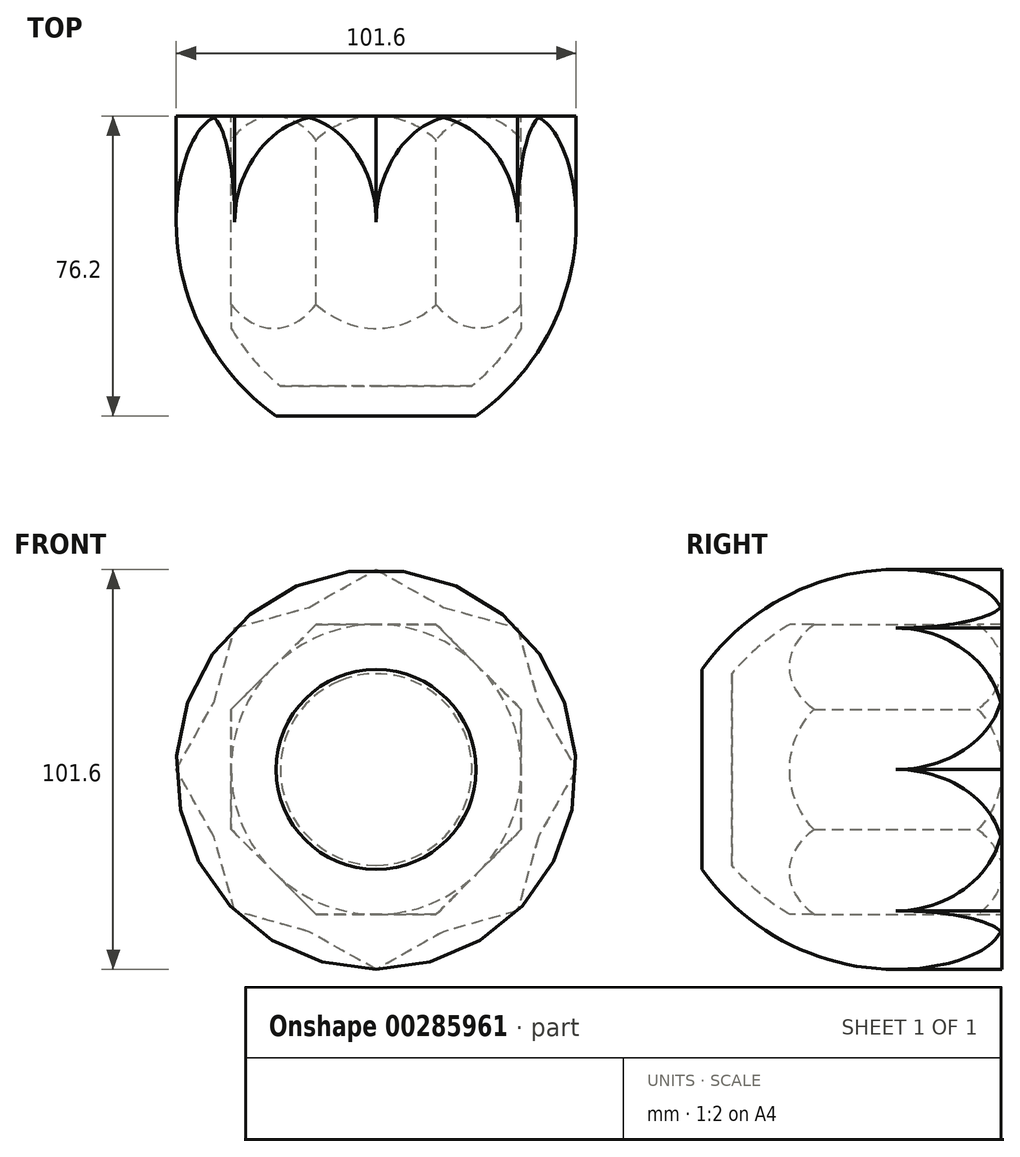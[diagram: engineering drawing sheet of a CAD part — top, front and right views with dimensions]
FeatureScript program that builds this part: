
annotation { "Feature Type Name" : "Feature", "Feature Type Description" : "" }
export const myFeature = defineFeature(function(context is Context, id is Id, definition is map)
    precondition{}
    {
        {
            var Q0;
            Q0=qCreatedBy(makeId("Top.planeOp"),FACE);
            var sketch = newSketch(context, id + "F0", { "sketchPlane" : qUnion([Q0])});
            skLineSegment(sketch, "E0", {"start": v(0, 0) * mm, "end": v(0, 76.2) * mm, "construction": true});
            skLineSegment(sketch, "E1", {"start": v(0, 76.2) * mm, "end": v(44.45, 76.2) * mm, "construction": true});
            skLineSegment(sketch, "E2", {"start": v(0, 0) * mm, "end": v(25.4, 0) * mm});
            skArc(sketch, "E3", {"start": v(25.4, 0) * mm, "mid": v(49, 34.58) * mm, "end": v(44.45, 76.2) * mm});
            skLineSegment(sketch, "E4", {"start": v(50.8, 0) * mm, "end": v(50.8, 76.2) * mm, "construction": true});
            skLineSegment(sketch, "E5", {"start": v(44.45, 76.2) * mm, "end": v(36.83, 76.2) * mm});
            skLineSegment(sketch, "E6", {"start": v(0, 0) * mm, "end": v(0, 7.62) * mm});
            skLineSegment(sketch, "E7", {"start": v(0, 7.62) * mm, "end": v(24.33, 7.62) * mm});
            skArc(sketch, "E8", {"start": v(24.33, 7.62) * mm, "mid": v(43.22, 39.6) * mm, "end": v(36.83, 76.2) * mm});
            skSolve(sketch);
        }
        {
            var Q0;
            Q0 = qSketchRegion(id + "F0", true);
            var Q1;
            Q1=sQuery(id+"F0.wireOp",EDGE,"E0");
            revolve(context, id + "F1", {"entities" : qUnion([Q0]), "axis" : qUnion([Q1]), "revolveType" : RevolveType.FULL});
        }
        {
            var Q0;
            Q0=makeQuery(id+"F1.opRevolve","SWEPT_FACE",FACE,{"disambiguationData":[OSD([sQuery(id+"F0.wireOp",EDGE,"E5")])]});
            var sketch = newSketch(context, id + "F2", { "sketchPlane" : qUnion([Q0])});
            skLineSegment(sketch, "E9", {"start": v(-24.89, 36.83) * mm, "end": v(24.89, 36.83) * mm});
            skLineSegment(sketch, "E10", {"start": v(24.89, 36.83) * mm, "end": v(0, 50.8) * mm});
            skLineSegment(sketch, "E11", {"start": v(0, 50.8) * mm, "end": v(-24.89, 36.83) * mm});
            skLineSegment(sketch, "E12.1.0", {"start": v(-43.64, 8.45) * mm, "end": v(-8.45, 43.64) * mm});
            skLineSegment(sketch, "E12.1.1", {"start": v(-8.45, 43.64) * mm, "end": v(-35.92, 35.92) * mm});
            skLineSegment(sketch, "E12.1.2", {"start": v(-35.92, 35.92) * mm, "end": v(-43.64, 8.45) * mm});
            skLineSegment(sketch, "E12.2.0", {"start": v(-36.83, -24.89) * mm, "end": v(-36.83, 24.89) * mm});
            skLineSegment(sketch, "E12.2.1", {"start": v(-36.83, 24.89) * mm, "end": v(-50.8, 0) * mm});
            skLineSegment(sketch, "E12.2.2", {"start": v(-50.8, 0) * mm, "end": v(-36.83, -24.89) * mm});
            skLineSegment(sketch, "E12.3.0", {"start": v(-8.45, -43.64) * mm, "end": v(-43.64, -8.45) * mm});
            skLineSegment(sketch, "E12.3.1", {"start": v(-43.64, -8.45) * mm, "end": v(-35.92, -35.92) * mm});
            skLineSegment(sketch, "E12.3.2", {"start": v(-35.92, -35.92) * mm, "end": v(-8.45, -43.64) * mm});
            skLineSegment(sketch, "E12.4.0", {"start": v(24.89, -36.83) * mm, "end": v(-24.89, -36.83) * mm});
            skLineSegment(sketch, "E12.4.1", {"start": v(-24.89, -36.83) * mm, "end": v(0, -50.8) * mm});
            skLineSegment(sketch, "E12.4.2", {"start": v(0, -50.8) * mm, "end": v(24.89, -36.83) * mm});
            skLineSegment(sketch, "E12.5.0", {"start": v(43.64, -8.45) * mm, "end": v(8.45, -43.64) * mm});
            skLineSegment(sketch, "E12.5.1", {"start": v(8.45, -43.64) * mm, "end": v(35.92, -35.92) * mm});
            skLineSegment(sketch, "E12.5.2", {"start": v(35.92, -35.92) * mm, "end": v(43.64, -8.45) * mm});
            skLineSegment(sketch, "E12.6.0", {"start": v(36.83, 24.89) * mm, "end": v(36.83, -24.89) * mm});
            skLineSegment(sketch, "E12.6.1", {"start": v(36.83, -24.89) * mm, "end": v(50.8, 0) * mm});
            skLineSegment(sketch, "E12.6.2", {"start": v(50.8, 0) * mm, "end": v(36.83, 24.89) * mm});
            skLineSegment(sketch, "E12.7.0", {"start": v(8.45, 43.64) * mm, "end": v(43.64, 8.45) * mm});
            skLineSegment(sketch, "E12.7.1", {"start": v(43.64, 8.45) * mm, "end": v(35.92, 35.92) * mm});
            skLineSegment(sketch, "E12.7.2", {"start": v(35.92, 35.92) * mm, "end": v(8.45, 43.64) * mm});
            skPoint(sketch, "E12.center", {"position": v(0, 0) * mm});
            skSolve(sketch);
        }
        {
            var Q0;
            Q0 = qSketchRegion(id + "F2", true);
            var Q1;
            Q1=makeQuery(id+"F1.opRevolve","SWEPT_FACE",FACE,{"disambiguationData":[OSD([sQuery(id+"F0.wireOp",EDGE,"E3")])]});
            extrude(context, id + "F3", {"entities" : qUnion([Q0]), "operationType" : NewBodyOperationType.ADD, "endBound" : BoundingType.UP_TO_SURFACE, "oppositeDirection" : true, "endBoundEntityFace" : qUnion([Q1]), "depth" : 25.4 * mm});
        }
    });
